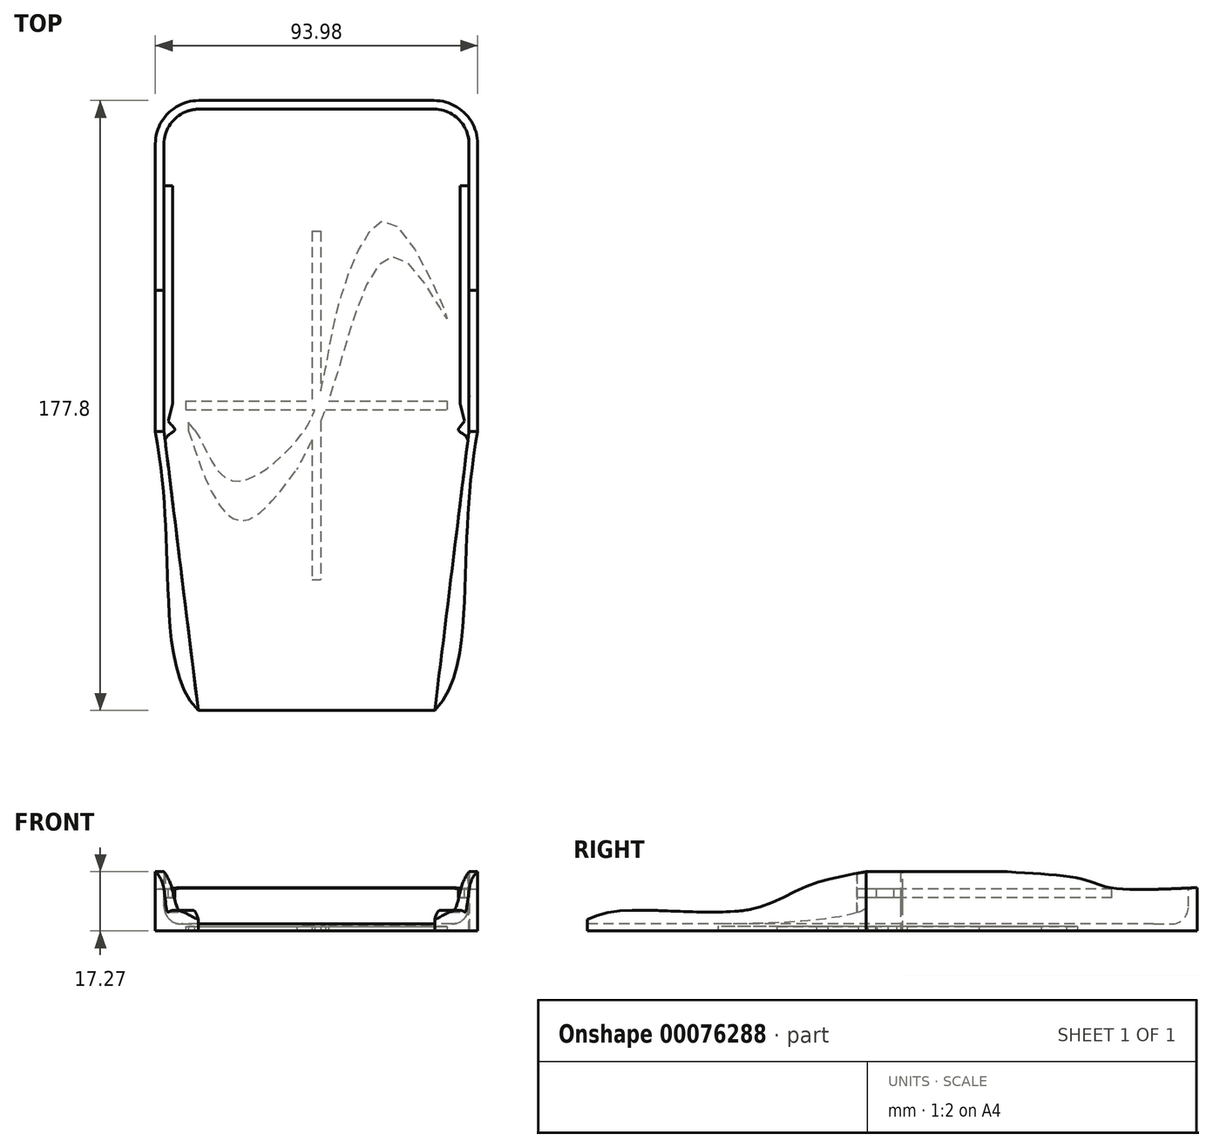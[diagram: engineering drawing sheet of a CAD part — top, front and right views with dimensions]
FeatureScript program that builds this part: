
annotation { "Feature Type Name" : "Feature", "Feature Type Description" : "" }
export const myFeature = defineFeature(function(context is Context, id is Id, definition is map)
    precondition{}
    {
        {
            var Q0;
            Q0=qCreatedBy(makeId("Top.planeOp"),FACE);
            var sketch = newSketch(context, id + "F0", { "sketchPlane" : qUnion([Q0])});
            skLineSegment(sketch, "E0.bottom", {"start": v(34.3, 88.9) * mm, "end": v(-34.3, 88.9) * mm});
            skLineSegment(sketch, "E0.top", {"start": v(46.99, -88.9) * mm, "end": v(-46.99, -88.9) * mm});
            skLineSegment(sketch, "E0.left", {"start": v(46.99, 76.2) * mm, "end": v(46.99, -88.9) * mm});
            skLineSegment(sketch, "E0.right", {"start": v(-47, 76.2) * mm, "end": v(-46.99, -88.9) * mm});
            skPoint(sketch, "E0.middle", {"position": v(0, 0) * mm});
            skPoint(sketch, "E1.visualSharp", {"position": v(-47, 88.9) * mm});
            skArc(sketch, "E1.filletArc", {"start": v(-34.3, 88.9) * mm, "mid": v(-43.27, 85.18) * mm, "end": v(-47, 76.2) * mm});
            skPoint(sketch, "E2.visualSharp", {"position": v(47, 88.9) * mm});
            skArc(sketch, "E2.filletArc", {"start": v(47, 76.2) * mm, "mid": v(43.27, 85.18) * mm, "end": v(34.3, 88.9) * mm});
            skLineSegment(sketch, "E3", {"start": v(0, -88.9) * mm, "end": v(-38.1, -88.9) * mm});
            skLineSegment(sketch, "E4", {"start": v(0, -88.9) * mm, "end": v(38.1, -88.9) * mm});
            skLineSegment(sketch, "E5", {"start": v(47, -88.9) * mm, "end": v(46.99, -7.62) * mm});
            skLineSegment(sketch, "E6.MirrorCS", {"start": v(-46.99, -88.9) * mm, "end": v(-47, -7.62) * mm});
            skPoint(sketch, "E7.1.internal.snap0", {"position": v(-46.99, -48.26) * mm});
            skFitSpline(sketch, "E7", {"points": [v(-46.99, -7.62) * mm, v(-43.45, -48.26) * mm, v(-34.48, -88.9) * mm, v(0, -95.06) * mm], "startDerivative": vector(20.85, -110.2) * mm, "endDerivative": vector(121.73, 3.89) * mm});
            skFitSpline(sketch, "E8.MirrorCS", {"points": [v(46.99, -7.62) * mm, v(43.45, -48.26) * mm, v(34.48, -88.9) * mm, v(0, -95.06) * mm], "startDerivative": vector(-20.85, -110.2) * mm, "endDerivative": vector(-121.73, 3.89) * mm});
            skLineSegment(sketch, "E9.bottom", {"start": v(-47, 66.55) * mm, "end": v(-44.45, 66.55) * mm});
            skLineSegment(sketch, "E9.left", {"start": v(-47, 66.55) * mm, "end": v(-46.99, -7.62) * mm});
            skLineSegment(sketch, "E10", {"start": v(53.05, 88.9) * mm, "end": v(-69.01, 88.9) * mm, "construction": true});
            skPoint(sketch, "E11.endSnap0", {"position": v(-46.99, 29.46) * mm});
            skLineSegment(sketch, "E12", {"start": v(-44.45, 66.55) * mm, "end": v(-44.45, 3.05) * mm});
            skLineSegment(sketch, "E13", {"start": v(-43.94, -2.03) * mm, "end": v(-43.94, -7.11) * mm});
            skPoint(sketch, "E14.1.internal.snap0", {"position": v(-43.94, -4.57) * mm});
            skLineSegment(sketch, "E15", {"start": v(0, 97.45) * mm, "end": v(0, -108.32) * mm, "construction": true});
            skLineSegment(sketch, "E16.MirrorCS", {"start": v(44.45, 66.55) * mm, "end": v(44.45, -2.03) * mm});
            skFitSpline(sketch, "E17.MirrorCS", {"points": [v(44.45, 3.05) * mm, v(42.16, -2.03) * mm], "startDerivative": vector(1.27, -5.08) * mm, "endDerivative": vector(1.27, -5.08) * mm});
            skFitSpline(sketch, "E18.MirrorCS", {"points": [v(42.16, -2.03) * mm, v(41, -4.57) * mm, v(42.16, -5.96) * mm, v(46.99, -7.62) * mm], "startDerivative": vector(-5.11, -7.46) * mm, "endDerivative": vector(3.51, -5.4) * mm});
            skSolve(sketch);
        }
        {
            var Q0;
            Q0=makeQuery(id+"F0.imprint","IMPRINT",FACE,{"disambiguationData":[TD([[makeQuery(id+"F0.imprint","IMPRINT",EDGE,{"derivedFrom":sQuery(id+"F0.wireOp",EDGE,"E0.bottom")}),1.0]])]});
            extrude(context, id + "F1", {"entities" : qUnion([Q0]), "depth" : 17.27 * mm});
        }
        {
            var Q0;
            Q0=makeQuery(id+"F1.opExtrude","CAP_FACE",FACE,{"disambiguationData":[OSD([sQuery(id+"F0.wireOp",EDGE,"E0.bottom"),sQuery(id+"F0.wireOp",EDGE,"E0.left"),sQuery(id+"F0.wireOp",EDGE,"E0.right"),sQuery(id+"F0.wireOp",EDGE,"E1.filletArc"),sQuery(id+"F0.wireOp",EDGE,"E2.filletArc"),sQuery(id+"F0.wireOp",EDGE,"E3"),sQuery(id+"F0.wireOp",EDGE,"E4"),sQuery(id+"F0.wireOp",EDGE,"E7"),sQuery(id+"F0.wireOp",EDGE,"E8.MirrorCS")])],"isStart":false});
            var sketch = newSketch(context, id + "F2", { "sketchPlane" : qUnion([Q0])});
            skLineSegment(sketch, "E19", {"start": v(-34.3, 86.36) * mm, "end": v(34.3, 86.36) * mm});
            skLineSegment(sketch, "E20", {"start": v(-44.45, 76.2) * mm, "end": v(-44.45, -7.62) * mm});
            skLineSegment(sketch, "E21", {"start": v(44.45, 76.2) * mm, "end": v(44.45, -7.62) * mm});
            skArc(sketch, "E22", {"start": v(-44.45, 76.2) * mm, "mid": v(-41.47, 83.38) * mm, "end": v(-34.3, 86.36) * mm});
            skArc(sketch, "E23", {"start": v(44.45, 76.2) * mm, "mid": v(41.47, 83.38) * mm, "end": v(34.3, 86.36) * mm});
            skLineSegment(sketch, "E24", {"start": v(-44.45, -7.62) * mm, "end": v(-44.45, -88.9) * mm, "construction": true});
            skLineSegment(sketch, "E25.MirrorCS", {"start": v(44.45, -7.62) * mm, "end": v(44.45, -88.9) * mm, "construction": true});
            skLineSegment(sketch, "E26", {"start": v(-44.45, -7.62) * mm, "end": v(-34.48, -88.9) * mm});
            skLineSegment(sketch, "E27.MirrorCS", {"start": v(44.45, -7.62) * mm, "end": v(34.48, -88.9) * mm});
            skLineSegment(sketch, "E28.bottom", {"start": v(-44.45, 64) * mm, "end": v(-41.91, 64) * mm});
            skLineSegment(sketch, "E28.top", {"start": v(-44.45, -4.57) * mm, "end": v(-41.9, -4.57) * mm});
            skLineSegment(sketch, "E28.left", {"start": v(-44.45, 64) * mm, "end": v(-44.45, -4.57) * mm});
            skLineSegment(sketch, "E28.right", {"start": v(-41.9, 64) * mm, "end": v(-41.9, -4.57) * mm});
            skLineSegment(sketch, "E29", {"start": v(48.82, 86.36) * mm, "end": v(-59.4, 86.36) * mm, "construction": true});
            skLineSegment(sketch, "E30", {"start": v(-35.18, 64) * mm, "end": v(-35.18, 0.5) * mm});
            skFitSpline(sketch, "E31", {"points": [v(-41.9, 0.5) * mm, v(-43.18, -4.57) * mm], "startDerivative": vector(-1.27, -5.08) * mm, "endDerivative": vector(-1.27, -5.08) * mm});
            skLineSegment(sketch, "E32", {"start": v(-44.97, -4.57) * mm, "end": v(-44.97, -9.65) * mm});
            skPoint(sketch, "E33.1.internal.snap0", {"position": v(-44.97, -7.11) * mm});
            skFitSpline(sketch, "E33", {"points": [v(-43.18, -4.57) * mm, v(-41.35, -7.11) * mm, v(-43.18, -8.6) * mm, v(-44.13, -10.2) * mm, v(-44.12, -10.29) * mm, v(-44.12, -10.28) * mm], "startDerivative": vector(5.13, -8.04) * mm, "endDerivative": vector(-0.1, 0.54) * mm});
            skLineSegment(sketch, "E34.MirrorCS", {"start": v(41.9, 64) * mm, "end": v(41.9, -4.57) * mm});
            skFitSpline(sketch, "E35.MirrorCS", {"points": [v(41.9, 0.5) * mm, v(43.18, -4.57) * mm], "startDerivative": vector(1.27, -5.08) * mm, "endDerivative": vector(1.27, -5.08) * mm});
            skFitSpline(sketch, "E36.MirrorCS", {"points": [v(43.18, -4.57) * mm, v(41.35, -7.11) * mm, v(43.18, -8.6) * mm, v(44.13, -10.2) * mm, v(44.12, -10.29) * mm, v(44.12, -10.28) * mm], "startDerivative": vector(-5.13, -8.04) * mm, "endDerivative": vector(0.1, 0.54) * mm});
            skLineSegment(sketch, "E37.MirrorCS", {"start": v(44.45, 64) * mm, "end": v(41.91, 64) * mm});
            skSolve(sketch);
        }
        {
            var Q0;
            Q0=makeQuery(id+"F2.imprint","IMPRINT",FACE,{"disambiguationData":[TD([[makeQuery(id+"F2.imprint","IMPRINT",EDGE,{"derivedFrom":sQuery(id+"F2.wireOp",EDGE,"E19")}),-1.0]])]});
            var Q1;
            {var subQ1=sQuery(id+"F2.wireOp",EDGE,"E28.bottom");Q1=makeQuery(id+"F2.imprint","IMPRINT",FACE,{"disambiguationData":[TD([[makeQuery(id+"F2.imprint","IMPRINT",EDGE,{"derivedFrom":subQ1}),-1.0]])]});}
            var Q2;
            {var subQ0=sQuery(id+"F2.wireOp",EDGE,"E26");var subQ1=sQuery(id+"F2.wireOp",EDGE,"E20");var subQ2=makeQuery(id+"F2.imprint","INTERSECT",VERTEX,{"derivedFrom":[subQ1,subQ0]});Q2=makeQuery(id+"F2.imprint","IMPRINT",FACE,{"disambiguationData":[TD([[makeQuery(id+"F2.imprint","IMPRINT",EDGE,{"disambiguationData":[TD([[subQ2,-1.0]])],"derivedFrom":subQ0}),1.0]])]});}
            var Q3;
            {var subQ3=sQuery(id+"F2.wireOp",EDGE,"E31");Q3=makeQuery(id+"F2.imprint","IMPRINT",FACE,{"disambiguationData":[TD([[makeQuery(id+"F2.imprint","IMPRINT",EDGE,{"derivedFrom":subQ3}),1.0]])]});}
            var Q4;
            {var subQ2=sQuery(id+"F2.wireOp",EDGE,"E35.MirrorCS");Q4=makeQuery(id+"F2.imprint","IMPRINT",FACE,{"disambiguationData":[TD([[makeQuery(id+"F2.imprint","IMPRINT",EDGE,{"derivedFrom":subQ2}),1.0]])]});}
            extrude(context, id + "F3", {"entities" : qUnion([Q0, Q1, Q2, Q3, Q4]), "operationType" : NewBodyOperationType.REMOVE, "oppositeDirection" : true, "depth" : 15.24 * mm});
        }
        {
            var Q0;
            Q0=makeQuery(id+"F1.opExtrude","SWEPT_FACE",FACE,{"disambiguationData":[OSD([sQuery(id+"F0.wireOp",EDGE,"E0.left")])]});
            var sketch = newSketch(context, id + "F4", { "sketchPlane" : qUnion([Q0])});
            skLineSegment(sketch, "E38", {"start": v(-90.42, 3.23) * mm, "end": v(-90.42, 2.54) * mm});
            skLineSegment(sketch, "E39", {"start": v(-90.42, 2.54) * mm, "end": v(-7.62, 2.54) * mm});
            skLineSegment(sketch, "E40", {"start": v(-90.42, 2.54) * mm, "end": v(-90.42, 0) * mm});
            skLineSegment(sketch, "E41", {"start": v(-7.62, 2.54) * mm, "end": v(-7.62, 17.27) * mm});
            skFitSpline(sketch, "E42", {"points": [v(-7.62, 17.27) * mm, v(-25.99, 12.69) * mm, v(-41.86, 6.2) * mm, v(-79.71, 5.87) * mm, v(-90.42, 2.54) * mm], "startDerivative": vector(-81.4, -14.51) * mm, "endDerivative": vector(-44.44, -23.04) * mm});
            skLineSegment(sketch, "E43", {"start": v(-7.62, 17.27) * mm, "end": v(-90.42, 17.27) * mm});
            skLineSegment(sketch, "E44", {"start": v(-90.42, 17.27) * mm, "end": v(-90.42, 3.23) * mm});
            skLineSegment(sketch, "E45", {"start": v(90.03, 0) * mm, "end": v(90.03, 12.7) * mm});
            skLineSegment(sketch, "E46", {"start": v(90.03, 12.7) * mm, "end": v(90.06, 17.27) * mm});
            skPoint(sketch, "E47.1.internal.snap0", {"position": v(90.04, 14.99) * mm});
            skFitSpline(sketch, "E47", {"points": [v(33.54, 17.27) * mm, v(55.9, 14.99) * mm, v(63.11, 12.7) * mm, v(90.03, 12.7) * mm], "startDerivative": vector(70.29, -4.08) * mm, "endDerivative": vector(78.4, 3.83) * mm});
            skLineSegment(sketch, "E48", {"start": v(33.54, 17.27) * mm, "end": v(90.06, 17.27) * mm});
            skSolve(sketch);
        }
        {
            var Q0;
            Q0=makeQuery(id+"F4.imprint","IMPRINT",FACE,{"disambiguationData":[TD([[makeQuery(id+"F4.imprint","IMPRINT",EDGE,{"derivedFrom":sQuery(id+"F4.wireOp",EDGE,"E38")}),1.0]])]});
            extrude(context, id + "F5", {"entities" : qUnion([Q0]), "operationType" : NewBodyOperationType.REMOVE, "oppositeDirection" : true, "depth" : 101.6 * mm});
        }
        {
            var Q0;
            {var subQ0=sQuery(id+"F4.wireOp",EDGE,"E48");var subQ1=sQuery(id+"F4.wireOp",EDGE,"E47");var subQ2=sQuery(id+"F0.wireOp",EDGE,"E0.left");var subQ3=makeQuery(id+"F4.imprint","INTERSECT",VERTEX,{"derivedFrom":[makeQuery(id+"F1.opExtrude","CAP_EDGE",EDGE,{"disambiguationData":[OSD([subQ2])],"isStart":false}),subQ1,subQ0]});Q0=makeQuery(id+"F4.imprint","IMPRINT",FACE,{"disambiguationData":[TD([[makeQuery(id+"F4.imprint","IMPRINT",EDGE,{"disambiguationData":[TD([[subQ3,-1.0]])],"derivedFrom":subQ1}),1.0]])]});}
            var Q1;
            {var subQ0=sQuery(id+"F4.wireOp",EDGE,"E46");Q1=makeQuery(id+"F4.imprint","IMPRINT",FACE,{"disambiguationData":[TD([[makeQuery(id+"F4.imprint","IMPRINT",EDGE,{"derivedFrom":subQ0}),1.0]])]});}
            extrude(context, id + "F6", {"entities" : qUnion([Q0, Q1]), "operationType" : NewBodyOperationType.REMOVE, "oppositeDirection" : true, "depth" : 101.6 * mm});
        }
        {
            var Q0;
            Q0=makeQuery(id+"F1.opExtrude","CAP_FACE",FACE,{"disambiguationData":[OSD([sQuery(id+"F0.wireOp",EDGE,"E0.bottom"),sQuery(id+"F0.wireOp",EDGE,"E0.left"),sQuery(id+"F0.wireOp",EDGE,"E0.right"),sQuery(id+"F0.wireOp",EDGE,"E1.filletArc"),sQuery(id+"F0.wireOp",EDGE,"E2.filletArc"),sQuery(id+"F0.wireOp",EDGE,"E3"),sQuery(id+"F0.wireOp",EDGE,"E4"),sQuery(id+"F0.wireOp",EDGE,"E7"),sQuery(id+"F0.wireOp",EDGE,"E8.MirrorCS")])],"isStart":true});
            var sketch = newSketch(context, id + "F7", { "sketchPlane" : qUnion([Q0])});
            skLineSegment(sketch, "E49.bottom", {"start": v(-1.27, -50.8) * mm, "end": v(1.27, -50.8) * mm});
            skLineSegment(sketch, "E49.top", {"start": v(-1.27, 50.8) * mm, "end": v(1.27, 50.8) * mm});
            skLineSegment(sketch, "E49.left", {"start": v(-1.27, -50.8) * mm, "end": v(-1.27, 50.8) * mm});
            skLineSegment(sketch, "E49.right", {"start": v(1.27, -50.8) * mm, "end": v(1.27, 50.8) * mm});
            skPoint(sketch, "E49.middle", {"position": v(0, 0) * mm});
            skLineSegment(sketch, "E50.bottom", {"start": v(-38.1, -1.27) * mm, "end": v(38.1, -1.27) * mm});
            skLineSegment(sketch, "E50.top", {"start": v(-38.1, 1.27) * mm, "end": v(38.1, 1.27) * mm});
            skLineSegment(sketch, "E50.left", {"start": v(-38.1, -1.27) * mm, "end": v(-38.1, 1.27) * mm});
            skLineSegment(sketch, "E50.right", {"start": v(38.1, -1.27) * mm, "end": v(38.1, 1.27) * mm});
            skFitSpline(sketch, "E51", {"points": [v(38.1, -25.33) * mm, v(25.85, -42.13) * mm, v(16.43, -38.58) * mm, v(3.5, -1.27) * mm, v(-5.78, 18.81) * mm, v(-18.36, 37.22) * mm, v(-31.2, 28.94) * mm, v(-37.33, 7.34) * mm, v(-35.64, 7.11) * mm, v(-26.05, 21.36) * mm, v(-9.93, 14.56) * mm, v(0, 0) * mm, v(5.22, -24.27) * mm, v(13.96, -48.37) * mm, v(22.49, -53.05) * mm, v(38.1, -25.33) * mm]});
            skLineSegment(sketch, "E52", {"start": v(-35.64, 7.11) * mm, "end": v(-37.33, 4.97) * mm});
            skLineSegment(sketch, "E53", {"start": v(-37.33, 4.97) * mm, "end": v(-37.33, 7.34) * mm});
            skFitSpline(sketch, "E54", {"points": [v(-37.33, 7.34) * mm, v(-27.93, 29.48) * mm, v(-20.4, 33.41) * mm, v(-5.78, 18.81) * mm], "startDerivative": vector(21.52, 64.95) * mm, "endDerivative": vector(41.76, -55.24) * mm});
            skLineSegment(sketch, "E55.bottom", {"start": v(-13.51, -64.7) * mm, "end": v(13.51, -64.7) * mm});
            skLineSegment(sketch, "E55.top", {"start": v(-13.51, -66.54) * mm, "end": v(13.51, -66.54) * mm});
            skLineSegment(sketch, "E55.left", {"start": v(-13.51, -64.7) * mm, "end": v(-13.51, -66.54) * mm});
            skLineSegment(sketch, "E55.right", {"start": v(13.51, -64.7) * mm, "end": v(13.51, -66.54) * mm});
            skPoint(sketch, "E55.middle", {"position": v(0, -65.62) * mm});
            skPoint(sketch, "E55.middle.positionSnap0", {"position": v(0, -50.8) * mm});
            skPoint(sketch, "E55.centerSnap0", {"position": v(0, -50.8) * mm});
            skLineSegment(sketch, "E56.bottom", {"start": v(13, -66.54) * mm, "end": v(12.64, -66.54) * mm});
            skLineSegment(sketch, "E56.top", {"start": v(13, -64.7) * mm, "end": v(12.64, -64.7) * mm});
            skLineSegment(sketch, "E56.left", {"start": v(13, -66.54) * mm, "end": v(13, -64.7) * mm});
            skLineSegment(sketch, "E56.right", {"start": v(12.64, -66.54) * mm, "end": v(12.64, -64.7) * mm});
            skArc(sketch, "E57", {"start": v(12.64, -65.62) * mm, "mid": v(12.18, -66.08) * mm, "end": v(12.64, -66.54) * mm});
            skArc(sketch, "E58", {"start": v(12.64, -64.7) * mm, "mid": v(12.18, -65.16) * mm, "end": v(12.64, -65.62) * mm});
            skCircle(sketch, "E59", {"center": v(11.14, -65.62) * mm, "radius": 0.77 * mm});
            skCircle(sketch, "E60", {"center": v(11.14, -65.62) * mm, "radius": 0.38 * mm});
            skLineSegment(sketch, "E61", {"start": v(10.26, -64.7) * mm, "end": v(9.77, -66.54) * mm});
            skLineSegment(sketch, "E62", {"start": v(9.77, -66.54) * mm, "end": v(9.48, -66.54) * mm});
            skLineSegment(sketch, "E63", {"start": v(9.48, -66.54) * mm, "end": v(9.25, -65.7) * mm});
            skLineSegment(sketch, "E64", {"start": v(9.98, -64.7) * mm, "end": v(9.67, -65.86) * mm});
            skLineSegment(sketch, "E65", {"start": v(9.67, -65.86) * mm, "end": v(9.5, -65.86) * mm});
            skLineSegment(sketch, "E66", {"start": v(9.5, -65.86) * mm, "end": v(9.36, -65.34) * mm});
            skLineSegment(sketch, "E67", {"start": v(9.25, -66.75) * mm, "end": v(9.25, -64.26) * mm, "construction": true});
            skLineSegment(sketch, "E68.MirrorCS", {"start": v(9.02, -66.54) * mm, "end": v(9.25, -65.7) * mm});
            skLineSegment(sketch, "E69.MirrorCS", {"start": v(8.23, -64.7) * mm, "end": v(8.72, -66.54) * mm});
            skLineSegment(sketch, "E70.MirrorCS", {"start": v(8.72, -66.54) * mm, "end": v(9.02, -66.54) * mm});
            skLineSegment(sketch, "E71.MirrorCS", {"start": v(8.52, -64.7) * mm, "end": v(8.83, -65.86) * mm});
            skLineSegment(sketch, "E72.MirrorCS", {"start": v(8.83, -65.86) * mm, "end": v(8.99, -65.86) * mm});
            skLineSegment(sketch, "E73.MirrorCS", {"start": v(8.99, -65.86) * mm, "end": v(9.13, -65.34) * mm});
            skLineSegment(sketch, "E74", {"start": v(9.36, -65.34) * mm, "end": v(9.13, -65.34) * mm});
            skLineSegment(sketch, "E75.bottom", {"start": v(5.72, -66.54) * mm, "end": v(5.21, -66.54) * mm});
            skLineSegment(sketch, "E75.top", {"start": v(5.72, -64.7) * mm, "end": v(5.21, -64.7) * mm});
            skLineSegment(sketch, "E75.left", {"start": v(5.72, -66.54) * mm, "end": v(5.72, -64.7) * mm});
            skLineSegment(sketch, "E75.right", {"start": v(5.21, -66.54) * mm, "end": v(5.21, -64.7) * mm});
            skLineSegment(sketch, "E76.bottom", {"start": v(4.64, -66.54) * mm, "end": v(4.34, -66.54) * mm});
            skLineSegment(sketch, "E76.top", {"start": v(4.64, -64.7) * mm, "end": v(4.34, -64.7) * mm});
            skLineSegment(sketch, "E76.left", {"start": v(4.64, -66.54) * mm, "end": v(4.64, -64.7) * mm});
            skLineSegment(sketch, "E76.right", {"start": v(4.34, -66.54) * mm, "end": v(4.34, -64.7) * mm});
            skArc(sketch, "E77", {"start": v(4.34, -64.7) * mm, "mid": v(3.42, -65.62) * mm, "end": v(4.34, -66.54) * mm});
            skArc(sketch, "E78", {"start": v(2.62, -65.62) * mm, "mid": v(1.7, -64.7) * mm, "end": v(0.8, -65.62) * mm});
            skPoint(sketch, "E78.startSnap0", {"position": v(3.42, -65.62) * mm});
            skPoint(sketch, "E78.centerSnap0", {"position": v(3.42, -65.62) * mm});
            skLineSegment(sketch, "E79", {"start": v(2.62, -65.62) * mm, "end": v(2.62, -66.54) * mm});
            skLineSegment(sketch, "E80", {"start": v(0.8, -65.62) * mm, "end": v(0.8, -66.54) * mm});
            skArc(sketch, "E81", {"start": v(2.26, -65.62) * mm, "mid": v(1.7, -65.07) * mm, "end": v(1.16, -65.62) * mm});
            skLineSegment(sketch, "E82", {"start": v(2.26, -65.62) * mm, "end": v(2.26, -66.54) * mm});
            skLineSegment(sketch, "E83", {"start": v(1.16, -65.62) * mm, "end": v(1.16, -66.54) * mm});
            skPoint(sketch, "E84.1.internal.snap0", {"position": v(0, -66.54) * mm});
            skFitSpline(sketch, "E84", {"points": [v(-0.82, -66.54) * mm, v(0, -66.2) * mm, v(0.35, -65.62) * mm, v(-0.38, -65.62) * mm, v(-0.78, -65.62) * mm, v(-0.69, -65.25) * mm, v(0, -64.7) * mm], "startDerivative": vector(4.32, 1.06) * mm, "endDerivative": vector(4.16, 2.56) * mm});
            skFitSpline(sketch, "E85", {"points": [v(-0.82, -66.4) * mm, v(-0.51, -66.3) * mm, v(-0.1, -66.07) * mm, v(0.1, -65.8) * mm, v(-0.25, -65.77) * mm, v(-0.67, -65.8) * mm, v(-0.9, -65.77) * mm, v(-0.96, -65.5) * mm, v(-0.82, -65.13) * mm, v(-0.25, -64.7) * mm], "startDerivative": vector(2.92, 0.91) * mm, "endDerivative": vector(4.4, 2.7) * mm});
            skLineSegment(sketch, "E86", {"start": v(-0.82, -66.4) * mm, "end": v(-0.82, -66.54) * mm});
            skLineSegment(sketch, "E87.bottom", {"start": v(-2.21, -66.54) * mm, "end": v(-2.52, -66.54) * mm});
            skLineSegment(sketch, "E87.top", {"start": v(-2.21, -64.7) * mm, "end": v(-2.52, -64.7) * mm});
            skLineSegment(sketch, "E87.left", {"start": v(-2.21, -66.54) * mm, "end": v(-2.21, -64.7) * mm});
            skLineSegment(sketch, "E87.right", {"start": v(-2.52, -66.54) * mm, "end": v(-2.52, -64.7) * mm});
            skLineSegment(sketch, "E88.bottom", {"start": v(-3.2, -65.95) * mm, "end": v(-1.54, -65.95) * mm});
            skLineSegment(sketch, "E88.top", {"start": v(-3.2, -66.22) * mm, "end": v(-1.54, -66.22) * mm});
            skLineSegment(sketch, "E88.left", {"start": v(-3.2, -65.95) * mm, "end": v(-3.2, -66.22) * mm});
            skLineSegment(sketch, "E88.right", {"start": v(-1.54, -65.95) * mm, "end": v(-1.54, -66.22) * mm});
            skPoint(sketch, "E88.middle", {"position": v(-2.37, -66.08) * mm});
            skPoint(sketch, "E88.middle.positionSnap0", {"position": v(-2.37, -64.7) * mm});
            skPoint(sketch, "E88.centerSnap0", {"position": v(-2.37, -64.7) * mm});
            skLineSegment(sketch, "E89.bottom", {"start": v(-3.94, -66.54) * mm, "end": v(-4.51, -66.54) * mm});
            skLineSegment(sketch, "E89.top", {"start": v(-3.94, -64.7) * mm, "end": v(-4.51, -64.7) * mm});
            skLineSegment(sketch, "E89.left", {"start": v(-3.94, -66.54) * mm, "end": v(-3.94, -64.7) * mm});
            skLineSegment(sketch, "E89.right", {"start": v(-4.51, -66.54) * mm, "end": v(-4.51, -64.7) * mm});
            skArc(sketch, "E90", {"start": v(-4.51, -65.62) * mm, "mid": v(-4.97, -66.08) * mm, "end": v(-4.51, -66.54) * mm});
            skLineSegment(sketch, "E91", {"start": v(-4.51, -65.62) * mm, "end": v(-5.4, -64.7) * mm});
            skLineSegment(sketch, "E92", {"start": v(-4.51, -65.38) * mm, "end": v(-5.17, -64.7) * mm});
            skLineSegment(sketch, "E93.bottom", {"start": v(-5.9, -66.54) * mm, "end": v(-6.35, -66.54) * mm});
            skLineSegment(sketch, "E93.top", {"start": v(-5.9, -64.7) * mm, "end": v(-6.35, -64.7) * mm});
            skLineSegment(sketch, "E93.left", {"start": v(-5.9, -66.54) * mm, "end": v(-5.9, -64.7) * mm});
            skLineSegment(sketch, "E93.right", {"start": v(-6.35, -66.54) * mm, "end": v(-6.35, -64.7) * mm});
            skLineSegment(sketch, "E94.bottom", {"start": v(-6.98, -66.54) * mm, "end": v(-7.25, -66.54) * mm});
            skLineSegment(sketch, "E94.top", {"start": v(-6.98, -64.7) * mm, "end": v(-7.25, -64.7) * mm});
            skLineSegment(sketch, "E94.left", {"start": v(-6.98, -66.54) * mm, "end": v(-6.98, -64.7) * mm});
            skLineSegment(sketch, "E94.right", {"start": v(-7.25, -66.54) * mm, "end": v(-7.25, -64.7) * mm});
            skLineSegment(sketch, "E95.bottom", {"start": v(-7.25, -66.54) * mm, "end": v(-8.04, -66.54) * mm});
            skLineSegment(sketch, "E95.top", {"start": v(-7.25, -66.26) * mm, "end": v(-8.04, -66.26) * mm});
            skLineSegment(sketch, "E95.left", {"start": v(-7.25, -66.54) * mm, "end": v(-7.25, -66.26) * mm});
            skLineSegment(sketch, "E95.right", {"start": v(-8.04, -66.54) * mm, "end": v(-8.04, -66.26) * mm});
            skPoint(sketch, "E96.oppositeSnap0", {"position": v(-7.25, -65.62) * mm});
            skLineSegment(sketch, "E96.bottom", {"start": v(-7.25, -65.87) * mm, "end": v(-8.04, -65.87) * mm});
            skLineSegment(sketch, "E96.top", {"start": v(-7.25, -65.62) * mm, "end": v(-8.04, -65.62) * mm});
            skLineSegment(sketch, "E96.left", {"start": v(-7.25, -65.87) * mm, "end": v(-7.25, -65.62) * mm});
            skLineSegment(sketch, "E96.right", {"start": v(-8.04, -65.87) * mm, "end": v(-8.04, -65.62) * mm});
            skLineSegment(sketch, "E97.bottom", {"start": v(-7.25, -64.7) * mm, "end": v(-8.04, -64.7) * mm});
            skLineSegment(sketch, "E97.top", {"start": v(-7.25, -64.98) * mm, "end": v(-8.04, -64.98) * mm});
            skLineSegment(sketch, "E97.left", {"start": v(-7.25, -64.7) * mm, "end": v(-7.25, -64.98) * mm});
            skLineSegment(sketch, "E97.right", {"start": v(-8.04, -64.7) * mm, "end": v(-8.04, -64.98) * mm});
            skFitSpline(sketch, "E98", {"points": [v(-9.34, -66.7) * mm, v(-8.52, -66.35) * mm, v(-8.16, -65.78) * mm, v(-8.9, -65.78) * mm, v(-9.3, -65.78) * mm, v(-9.2, -65.41) * mm, v(-8.52, -64.86) * mm], "startDerivative": vector(4.32, 1.06) * mm, "endDerivative": vector(4.16, 2.56) * mm});
            skFitSpline(sketch, "E99", {"points": [v(-9.34, -66.56) * mm, v(-9.03, -66.46) * mm, v(-8.62, -66.23) * mm, v(-8.42, -65.96) * mm, v(-8.77, -65.93) * mm, v(-9.18, -65.97) * mm, v(-9.41, -65.93) * mm, v(-9.48, -65.66) * mm, v(-9.34, -65.3) * mm, v(-8.77, -64.86) * mm], "startDerivative": vector(2.92, 0.91) * mm, "endDerivative": vector(4.4, 2.7) * mm});
            skLineSegment(sketch, "E100", {"start": v(-9.34, -66.56) * mm, "end": v(-9.34, -66.7) * mm});
            skLineSegment(sketch, "E101", {"start": v(-8.52, -64.86) * mm, "end": v(-8.77, -64.86) * mm});
            skLineSegment(sketch, "E102.bottom", {"start": v(16.78, -64.7) * mm, "end": v(19.43, -64.7) * mm});
            skLineSegment(sketch, "E102.top", {"start": v(16.78, -67.84) * mm, "end": v(19.43, -67.84) * mm});
            skLineSegment(sketch, "E102.left", {"start": v(16.78, -64.7) * mm, "end": v(16.78, -67.84) * mm});
            skLineSegment(sketch, "E102.right", {"start": v(19.43, -64.7) * mm, "end": v(19.43, -67.84) * mm});
            skLineSegment(sketch, "E103.bottom", {"start": v(19, -67.84) * mm, "end": v(17.3, -67.84) * mm});
            skLineSegment(sketch, "E103.top", {"start": v(19, -69.3) * mm, "end": v(17.3, -69.3) * mm});
            skLineSegment(sketch, "E103.left", {"start": v(19, -67.84) * mm, "end": v(19, -69.3) * mm});
            skLineSegment(sketch, "E103.right", {"start": v(17.3, -67.84) * mm, "end": v(17.3, -69.3) * mm});
            skLineSegment(sketch, "E104.bottom", {"start": v(18.65, -69.3) * mm, "end": v(17.55, -69.3) * mm});
            skLineSegment(sketch, "E104.top", {"start": v(18.65, -69.83) * mm, "end": v(17.55, -69.83) * mm});
            skLineSegment(sketch, "E104.left", {"start": v(18.65, -69.3) * mm, "end": v(18.65, -69.83) * mm});
            skLineSegment(sketch, "E104.right", {"start": v(17.55, -69.3) * mm, "end": v(17.55, -69.83) * mm});
            skArc(sketch, "E105", {"start": v(17.55, -69.83) * mm, "mid": v(18.1, -70.39) * mm, "end": v(18.65, -69.83) * mm});
            skLineSegment(sketch, "E106.bottom", {"start": v(18.82, -67.84) * mm, "end": v(18.57, -67.84) * mm});
            skLineSegment(sketch, "E106.top", {"start": v(18.82, -68.7) * mm, "end": v(18.57, -68.7) * mm});
            skLineSegment(sketch, "E106.left", {"start": v(18.82, -67.84) * mm, "end": v(18.82, -68.7) * mm});
            skLineSegment(sketch, "E106.right", {"start": v(18.57, -67.84) * mm, "end": v(18.57, -68.7) * mm});
            skLineSegment(sketch, "E107.bottom", {"start": v(18.45, -67.84) * mm, "end": v(18.2, -67.84) * mm});
            skLineSegment(sketch, "E107.top", {"start": v(18.45, -68.7) * mm, "end": v(18.2, -68.7) * mm});
            skLineSegment(sketch, "E107.left", {"start": v(18.45, -67.84) * mm, "end": v(18.45, -68.7) * mm});
            skLineSegment(sketch, "E107.right", {"start": v(18.2, -67.84) * mm, "end": v(18.2, -68.7) * mm});
            skLineSegment(sketch, "E108", {"start": v(18.1, -64.17) * mm, "end": v(18.1, -66.64) * mm, "construction": true});
            skPoint(sketch, "E108.startSnap0", {"position": v(18.1, -64.7) * mm});
            skLineSegment(sketch, "E109.MirrorCS", {"start": v(18, -67.84) * mm, "end": v(18, -68.7) * mm});
            skLineSegment(sketch, "E110.MirrorCS", {"start": v(17.75, -67.84) * mm, "end": v(17.75, -68.7) * mm});
            skLineSegment(sketch, "E111.MirrorCS", {"start": v(17.63, -67.84) * mm, "end": v(17.63, -68.7) * mm});
            skLineSegment(sketch, "E112.MirrorCS", {"start": v(17.38, -68.7) * mm, "end": v(17.63, -68.7) * mm});
            skLineSegment(sketch, "E113.MirrorCS", {"start": v(17.38, -67.84) * mm, "end": v(17.38, -68.7) * mm});
            skLineSegment(sketch, "E114.MirrorCS", {"start": v(17.75, -68.7) * mm, "end": v(18, -68.7) * mm});
            skArc(sketch, "E115", {"start": v(18.57, -68.7) * mm, "mid": v(18.7, -68.84) * mm, "end": v(18.82, -68.7) * mm});
            skArc(sketch, "E116", {"start": v(18.2, -68.7) * mm, "mid": v(18.32, -68.84) * mm, "end": v(18.45, -68.7) * mm});
            skArc(sketch, "E117", {"start": v(17.75, -68.7) * mm, "mid": v(17.88, -68.84) * mm, "end": v(18, -68.7) * mm});
            skArc(sketch, "E118", {"start": v(17.38, -68.7) * mm, "mid": v(17.5, -68.84) * mm, "end": v(17.63, -68.7) * mm});
            skLineSegment(sketch, "E119.bottom", {"start": v(18.53, -69.3) * mm, "end": v(18.4, -69.3) * mm});
            skLineSegment(sketch, "E119.top", {"start": v(18.53, -69.72) * mm, "end": v(18.4, -69.72) * mm});
            skLineSegment(sketch, "E119.left", {"start": v(18.53, -69.3) * mm, "end": v(18.53, -69.72) * mm});
            skLineSegment(sketch, "E119.right", {"start": v(18.4, -69.3) * mm, "end": v(18.4, -69.72) * mm});
            skLineSegment(sketch, "E120.bottom", {"start": v(18.32, -69.3) * mm, "end": v(18.2, -69.3) * mm});
            skLineSegment(sketch, "E120.top", {"start": v(18.32, -69.72) * mm, "end": v(18.2, -69.72) * mm});
            skLineSegment(sketch, "E120.left", {"start": v(18.32, -69.3) * mm, "end": v(18.32, -69.72) * mm});
            skLineSegment(sketch, "E120.right", {"start": v(18.2, -69.3) * mm, "end": v(18.2, -69.72) * mm});
            skLineSegment(sketch, "E121.MirrorCS", {"start": v(18, -69.29) * mm, "end": v(18, -69.72) * mm});
            skLineSegment(sketch, "E122.MirrorCS", {"start": v(17.88, -69.72) * mm, "end": v(18, -69.72) * mm});
            skLineSegment(sketch, "E123.MirrorCS", {"start": v(17.88, -69.29) * mm, "end": v(17.88, -69.72) * mm});
            skLineSegment(sketch, "E124.MirrorCS", {"start": v(17.8, -69.29) * mm, "end": v(17.8, -69.72) * mm});
            skLineSegment(sketch, "E125.MirrorCS", {"start": v(17.67, -69.72) * mm, "end": v(17.8, -69.72) * mm});
            skLineSegment(sketch, "E126.MirrorCS", {"start": v(17.67, -69.29) * mm, "end": v(17.67, -69.72) * mm});
            skArc(sketch, "E127", {"start": v(18.4, -69.72) * mm, "mid": v(18.46, -69.78) * mm, "end": v(18.53, -69.72) * mm});
            skArc(sketch, "E128", {"start": v(18.2, -69.72) * mm, "mid": v(18.26, -69.78) * mm, "end": v(18.32, -69.72) * mm});
            skArc(sketch, "E129", {"start": v(17.88, -69.72) * mm, "mid": v(17.94, -69.78) * mm, "end": v(18, -69.72) * mm});
            skArc(sketch, "E130", {"start": v(17.67, -69.72) * mm, "mid": v(17.74, -69.78) * mm, "end": v(17.8, -69.72) * mm});
            skLineSegment(sketch, "E131.bottom", {"start": v(18.06, -70.77) * mm, "end": v(18.14, -70.77) * mm});
            skLineSegment(sketch, "E131.top", {"start": v(18.06, -70) * mm, "end": v(18.14, -70) * mm});
            skLineSegment(sketch, "E131.left", {"start": v(18.06, -70.77) * mm, "end": v(18.06, -70) * mm});
            skLineSegment(sketch, "E131.right", {"start": v(18.14, -70.77) * mm, "end": v(18.14, -70) * mm});
            skPoint(sketch, "E131.middle", {"position": v(18.1, -70.39) * mm});
            skPoint(sketch, "E132.middle", {"position": v(18.1, -70.7) * mm});
            skLineSegment(sketch, "E133.bottom", {"start": v(17.93, -70.63) * mm, "end": v(18.27, -70.63) * mm});
            skLineSegment(sketch, "E133.top", {"start": v(17.93, -70.56) * mm, "end": v(18.27, -70.56) * mm});
            skLineSegment(sketch, "E133.left", {"start": v(17.93, -70.63) * mm, "end": v(17.93, -70.56) * mm});
            skLineSegment(sketch, "E133.right", {"start": v(18.27, -70.63) * mm, "end": v(18.27, -70.56) * mm});
            skPoint(sketch, "E133.middle", {"position": v(18.1, -70.6) * mm});
            skSolve(sketch);
        }
        {
            var Q0;
            {var subQ0=sQuery(id+"F7.wireOp",EDGE,"E52");Q0=makeQuery(id+"F7.imprint","IMPRINT",FACE,{"disambiguationData":[TD([[makeQuery(id+"F7.imprint","IMPRINT",EDGE,{"derivedFrom":subQ0}),-1.0]])]});}
            var Q1;
            {var subQ0=sQuery(id+"F7.wireOp",EDGE,"E51");var subQ1=sQuery(id+"F7.wireOp",EDGE,"E49.right");var subQ2=makeQuery(id+"F7.imprint","INTERSECT",VERTEX,{"disambiguationData":[OD(0.0)],"derivedFrom":[subQ1,subQ0]});Q1=makeQuery(id+"F7.imprint","IMPRINT",FACE,{"disambiguationData":[TD([[makeQuery(id+"F7.imprint","IMPRINT",EDGE,{"disambiguationData":[TD([[subQ2,-1.0]])],"derivedFrom":subQ1}),-1.0]])]});}
            var Q2;
            {var subQ3=sQuery(id+"F7.wireOp",EDGE,"E51");var subQ5=sQuery(id+"F7.wireOp",EDGE,"E49.left");var subQ8=makeQuery(id+"F7.imprint","INTERSECT",VERTEX,{"disambiguationData":[OD(0.0)],"derivedFrom":[subQ5,subQ3]});Q2=makeQuery(id+"F7.imprint","IMPRINT",FACE,{"disambiguationData":[TD([[makeQuery(id+"F7.imprint","IMPRINT",EDGE,{"disambiguationData":[TD([[subQ8,-1.0]])],"derivedFrom":subQ5}),-1.0]])]});}
            var Q3;
            {var subQ0=sQuery(id+"F7.wireOp",EDGE,"E50.top");var subQ1=sQuery(id+"F7.wireOp",EDGE,"E49.right");var subQ2=makeQuery(id+"F7.imprint","INTERSECT",VERTEX,{"derivedFrom":[subQ1,subQ0]});Q3=makeQuery(id+"F7.imprint","IMPRINT",FACE,{"disambiguationData":[TD([[makeQuery(id+"F7.imprint","IMPRINT",EDGE,{"disambiguationData":[TD([[subQ2,-1.0]])],"derivedFrom":subQ1}),-1.0]])]});}
            var Q4;
            {var subQ0=sQuery(id+"F7.wireOp",EDGE,"E51");var subQ1=sQuery(id+"F7.wireOp",EDGE,"E49.right");var subQ2=makeQuery(id+"F7.imprint","INTERSECT",VERTEX,{"disambiguationData":[OD(0.0)],"derivedFrom":[subQ1,subQ0]});Q4=makeQuery(id+"F7.imprint","IMPRINT",FACE,{"disambiguationData":[TD([[makeQuery(id+"F7.imprint","IMPRINT",EDGE,{"disambiguationData":[TD([[subQ2,-1.0]])],"derivedFrom":subQ1}),1.0]])]});}
            var Q5;
            {var subQ0=sQuery(id+"F7.wireOp",EDGE,"E51");var subQ1=sQuery(id+"F7.wireOp",EDGE,"E49.left");var subQ2=makeQuery(id+"F7.imprint","INTERSECT",VERTEX,{"disambiguationData":[OD(0.0)],"derivedFrom":[subQ1,subQ0]});Q5=makeQuery(id+"F7.imprint","IMPRINT",FACE,{"disambiguationData":[TD([[makeQuery(id+"F7.imprint","IMPRINT",EDGE,{"disambiguationData":[TD([[subQ2,-1.0]])],"derivedFrom":subQ1}),1.0]])]});}
            var Q6;
            {var subQ0=sQuery(id+"F7.wireOp",EDGE,"E50.bottom");var subQ1=sQuery(id+"F7.wireOp",EDGE,"E49.right");var subQ2=makeQuery(id+"F7.imprint","INTERSECT",VERTEX,{"derivedFrom":[subQ1,subQ0]});Q6=makeQuery(id+"F7.imprint","IMPRINT",FACE,{"disambiguationData":[TD([[makeQuery(id+"F7.imprint","IMPRINT",EDGE,{"disambiguationData":[TD([[subQ2,-1.0]])],"derivedFrom":subQ1}),-1.0]])]});}
            var Q7;
            {var subQ0=sQuery(id+"F7.wireOp",EDGE,"E50.bottom");var subQ1=sQuery(id+"F7.wireOp",EDGE,"E49.right");var subQ2=makeQuery(id+"F7.imprint","INTERSECT",VERTEX,{"derivedFrom":[subQ1,subQ0]});Q7=makeQuery(id+"F7.imprint","IMPRINT",FACE,{"disambiguationData":[TD([[makeQuery(id+"F7.imprint","IMPRINT",EDGE,{"disambiguationData":[TD([[subQ2,-1.0]])],"derivedFrom":subQ1}),1.0]])]});}
            var Q8;
            {var subQ1=sQuery(id+"F7.wireOp",EDGE,"E49.bottom");Q8=makeQuery(id+"F7.imprint","IMPRINT",FACE,{"disambiguationData":[TD([[makeQuery(id+"F7.imprint","IMPRINT",EDGE,{"derivedFrom":subQ1}),1.0]])]});}
            var Q9;
            {var subQ0=sQuery(id+"F7.wireOp",EDGE,"E50.right");Q9=makeQuery(id+"F7.imprint","IMPRINT",FACE,{"disambiguationData":[TD([[makeQuery(id+"F7.imprint","IMPRINT",EDGE,{"derivedFrom":subQ0}),1.0]])]});}
            var Q10;
            {var subQ0=sQuery(id+"F7.wireOp",EDGE,"E49.top");Q10=makeQuery(id+"F7.imprint","IMPRINT",FACE,{"disambiguationData":[TD([[makeQuery(id+"F7.imprint","IMPRINT",EDGE,{"derivedFrom":subQ0}),-1.0]])]});}
            var Q11;
            {var subQ5=sQuery(id+"F7.wireOp",EDGE,"E50.left");Q11=makeQuery(id+"F7.imprint","IMPRINT",FACE,{"disambiguationData":[TD([[makeQuery(id+"F7.imprint","IMPRINT",EDGE,{"derivedFrom":subQ5}),-1.0]])]});}
            var Q12;
            {var subQ0=sQuery(id+"F7.wireOp",EDGE,"E50.bottom");var subQ1=sQuery(id+"F7.wireOp",EDGE,"E49.left");var subQ2=makeQuery(id+"F7.imprint","INTERSECT",VERTEX,{"derivedFrom":[subQ1,subQ0]});Q12=makeQuery(id+"F7.imprint","IMPRINT",FACE,{"disambiguationData":[TD([[makeQuery(id+"F7.imprint","IMPRINT",EDGE,{"disambiguationData":[TD([[subQ2,-1.0]])],"derivedFrom":subQ1}),-1.0]])]});}
            extrude(context, id + "F8", {"entities" : qUnion([Q0, Q1, Q2, Q3, Q4, Q5, Q6, Q7, Q8, Q9, Q10, Q11, Q12]), "operationType" : NewBodyOperationType.REMOVE, "oppositeDirection" : true, "depth" : 1.27 * mm});
        }
        {
            var Q0;
            {var subQ1=sQuery(id+"F2.wireOp",EDGE,"E28.bottom");Q0=makeQuery(id+"F2.imprint","IMPRINT",FACE,{"disambiguationData":[TD([[makeQuery(id+"F2.imprint","IMPRINT",EDGE,{"derivedFrom":subQ1}),-1.0]])]});}
            var Q1;
            {var subQ0=sQuery(id+"F2.wireOp",EDGE,"E26");var subQ1=sQuery(id+"F2.wireOp",EDGE,"E20");var subQ2=makeQuery(id+"F2.imprint","INTERSECT",VERTEX,{"derivedFrom":[subQ1,subQ0]});Q1=makeQuery(id+"F2.imprint","IMPRINT",FACE,{"disambiguationData":[TD([[makeQuery(id+"F2.imprint","IMPRINT",EDGE,{"disambiguationData":[TD([[subQ2,-1.0]])],"derivedFrom":subQ0}),1.0]])]});}
            var Q2;
            {var subQ2=sQuery(id+"F2.wireOp",EDGE,"E35.MirrorCS");Q2=makeQuery(id+"F2.imprint","IMPRINT",FACE,{"disambiguationData":[TD([[makeQuery(id+"F2.imprint","IMPRINT",EDGE,{"derivedFrom":subQ2}),1.0]])]});}
            extrude(context, id + "F9", {"entities" : qUnion([Q0, Q1, Q2]), "operationType" : NewBodyOperationType.ADD, "oppositeDirection" : true, "depth" : 7.62 * mm, "hasSecondDirection" : true, "secondDirectionOppositeDirection" : true, "secondDirectionDepth" : 5.08 * mm});
        }
        {
            var Q0;
            Q0=makeQuery(id+"F3.boolean.opBoolean","COPY",EDGE,{"derivedFrom":makeQuery(id+"F3.opExtrude","CAP_EDGE",EDGE,{"disambiguationData":[OSD([sQuery(id+"F2.wireOp",EDGE,"E20"),sQuery(id+"F2.wireOp",EDGE,"E28.left")])],"isStart":false})});
            var Q1;
            Q1=makeQuery(id+"F1.opExtrude","CAP_EDGE",EDGE,{"disambiguationData":[OSD([sQuery(id+"F0.wireOp",EDGE,"E3"),sQuery(id+"F0.wireOp",EDGE,"E4")])],"isStart":true});
            fillet(context, id + "F10", {"entities" : qUnion([Q0, Q1]), "radius" : 5.08 * mm, "tangentPropagation" : true, "allowEdgeOverflow" : false});
        }
    });
